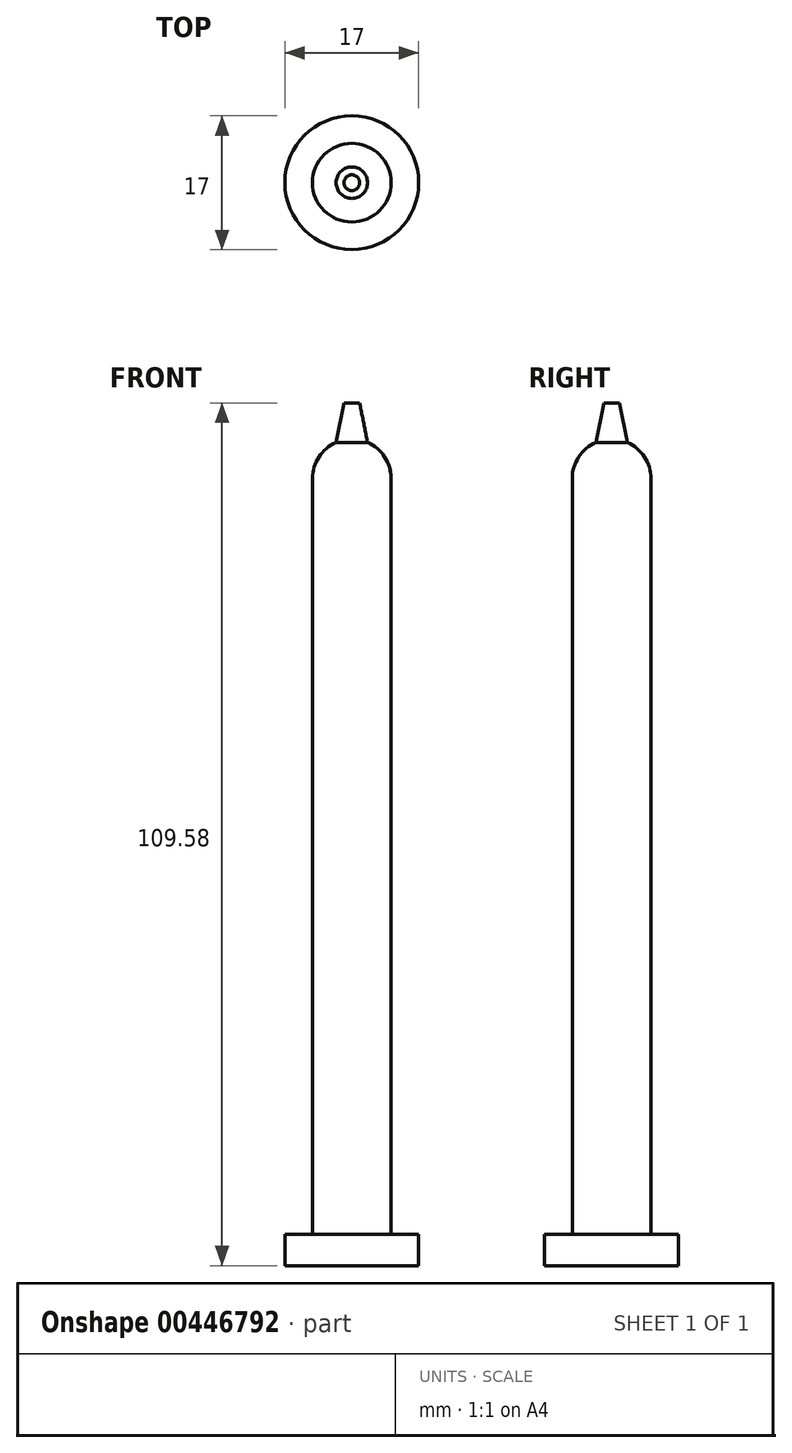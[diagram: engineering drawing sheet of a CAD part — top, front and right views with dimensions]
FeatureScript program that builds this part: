
annotation { "Feature Type Name" : "Feature", "Feature Type Description" : "" }
export const myFeature = defineFeature(function(context is Context, id is Id, definition is map)
    precondition{}
    {
        {
            var Q0;
            Q0=qCreatedBy(makeId("Top.planeOp"),FACE);
            var sketch = newSketch(context, id + "F0", { "sketchPlane" : qUnion([Q0])});
            skCircle(sketch, "E0", {"center": v(0, 0) * mm, "radius": 8.5 * mm});
            skSolve(sketch);
        }
        {
            var Q0;
            Q0=qSketchRegion(id+"F0",true);
            extrude(context, id + "F1", {"entities" : qUnion([Q0]), "depth" : 4 * mm});
        }
        {
            var Q0;
            Q0=qCreatedBy(makeId("Top.planeOp"),FACE);
            var sketch = newSketch(context, id + "F2", { "sketchPlane" : qUnion([Q0])});
            skCircle(sketch, "E1", {"center": v(0, 0) * mm, "radius": 5 * mm});
            skSolve(sketch);
        }
        {
            var Q0;
            Q0=qSketchRegion(id+"F2",true);
            extrude(context, id + "F3", {"entities" : qUnion([Q0]), "operationType" : NewBodyOperationType.ADD, "depth" : 100 * mm});
        }
        {
            var Q0;
            Q0=qCreatedBy(makeId("Right.planeOp"),FACE);
            var sketch = newSketch(context, id + "F4", { "sketchPlane" : qUnion([Q0])});
            skLineSegment(sketch, "E2", {"start": v(0, 100) * mm, "end": v(5, 100) * mm});
            skArc(sketch, "E3", {"start": v(5, 100) * mm, "mid": v(3.54, 103.54) * mm, "end": v(0, 105) * mm});
            skLineSegment(sketch, "E4", {"start": v(0, 109.58) * mm, "end": v(1, 109.58) * mm});
            skLineSegment(sketch, "E5", {"start": v(1, 109.58) * mm, "end": v(2, 104.58) * mm});
            skLineSegment(sketch, "E6", {"start": v(2, 104.58) * mm, "end": v(0, 104.58) * mm});
            skLineSegment(sketch, "E7", {"start": v(0, 109.58) * mm, "end": v(0, 100) * mm});
            skSolve(sketch);
        }
        {
            var Q0;
            {var subQ0=sQuery(id+"F4.wireOp",EDGE,"E2");Q0=makeQuery(id+"F4.imprint","IMPRINT",FACE,{"disambiguationData":[TD([[makeQuery(id+"F4.imprint","IMPRINT",EDGE,{"derivedFrom":subQ0}),1.0]])]});}
            var Q1;
            Q1=sQuery(id+"F4.wireOp",EDGE,"E7");
            revolve(context, id + "F5", {"operationType" : NewBodyOperationType.ADD, "entities" : qUnion([Q0]), "axis" : qUnion([Q1]), "revolveType" : RevolveType.FULL});
        }
        {
            var Q0;
            {var subQ4=sQuery(id+"F4.wireOp",EDGE,"E4");Q0=makeQuery(id+"F4.imprint","IMPRINT",FACE,{"disambiguationData":[TD([[makeQuery(id+"F4.imprint","IMPRINT",EDGE,{"derivedFrom":subQ4}),-1.0]])]});}
            var Q1;
            {var subQ3=sQuery(id+"F4.wireOp",EDGE,"E6");Q1=makeQuery(id+"F4.imprint","IMPRINT",FACE,{"disambiguationData":[TD([[makeQuery(id+"F4.imprint","IMPRINT",EDGE,{"derivedFrom":subQ3}),-1.0]])]});}
            var Q2;
            Q2=sQuery(id+"F4.wireOp",EDGE,"E7");
            revolve(context, id + "F6", {"operationType" : NewBodyOperationType.ADD, "entities" : qUnion([Q0, Q1]), "axis" : qUnion([Q2]), "revolveType" : RevolveType.FULL});
        }
    });
